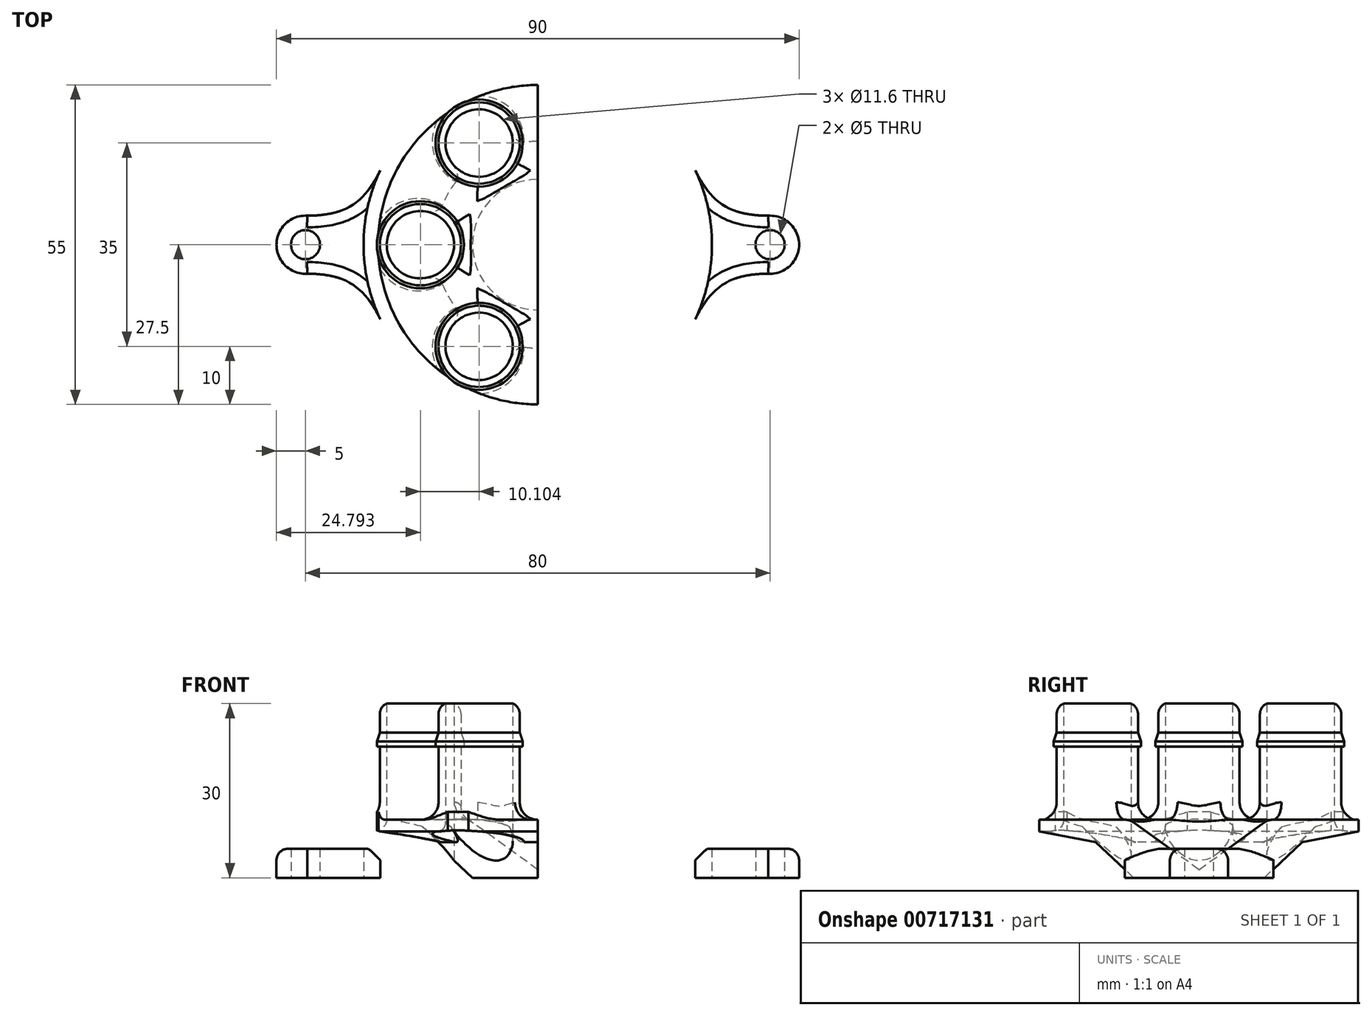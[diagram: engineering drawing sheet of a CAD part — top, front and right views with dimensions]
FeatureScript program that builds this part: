
annotation { "Feature Type Name" : "Feature", "Feature Type Description" : "" }
export const myFeature = defineFeature(function(context is Context, id is Id, definition is map)
    precondition{}
    {
        {
            var Q0;
            Q0=qCreatedBy(makeId("Top.planeOp"),FACE);
            var sketch = newSketch(context, id + "F0", { "sketchPlane" : qUnion([Q0])});
            skLineSegment(sketch, "E0", {"start": v(0, 45.94) * mm, "end": v(0, -54.06) * mm});
            skCircle(sketch, "E1.cCircle", {"center": v(0, 0) * mm, "radius": 17.5 * mm, "construction": true});
            skLineSegment(sketch, "E1.0", {"start": v(-10.1, -17.5) * mm, "end": v(-20.2, 0) * mm, "construction": true});
            skLineSegment(sketch, "E1.1", {"start": v(-20.2, 0) * mm, "end": v(-10.1, 17.5) * mm, "construction": true});
            skLineSegment(sketch, "E1.2", {"start": v(-10.1, 17.5) * mm, "end": v(10.1, 17.5) * mm, "construction": true});
            skLineSegment(sketch, "E1.3", {"start": v(10.1, 17.5) * mm, "end": v(20.2, 0) * mm, "construction": true});
            skLineSegment(sketch, "E1.4", {"start": v(20.2, 0) * mm, "end": v(10.1, -17.5) * mm, "construction": true});
            skLineSegment(sketch, "E1.5", {"start": v(10.1, -17.5) * mm, "end": v(-10.1, -17.5) * mm, "construction": true});
            skPoint(sketch, "E1.0.midPoint", {"position": v(-15.16, -8.75) * mm});
            skCircle(sketch, "E2", {"center": v(-20.2, 0) * mm, "radius": 7 * mm});
            skCircle(sketch, "E3", {"center": v(-10.1, -17.5) * mm, "radius": 7 * mm});
            skCircle(sketch, "E4", {"center": v(-10.1, 17.5) * mm, "radius": 7 * mm});
            skCircle(sketch, "E5", {"center": v(0, 0) * mm, "radius": 27.5 * mm});
            skCircle(sketch, "E6", {"center": v(-20.2, 0) * mm, "radius": 5.8 * mm});
            skCircle(sketch, "E7", {"center": v(-10.1, 17.5) * mm, "radius": 5.8 * mm});
            skCircle(sketch, "E8", {"center": v(-10.1, -17.5) * mm, "radius": 5.8 * mm});
            skCircle(sketch, "E9", {"center": v(0, 0) * mm, "radius": 30 * mm});
            skCircle(sketch, "E10", {"center": v(0, 0) * mm, "radius": 40 * mm, "construction": true});
            skCircle(sketch, "E11", {"center": v(-40, 0) * mm, "radius": 2.5 * mm});
            skCircle(sketch, "E12", {"center": v(-40, 0) * mm, "radius": 5 * mm});
            skFitSpline(sketch, "E13", {"points": [v(-39.69, -5) * mm, v(-27.13, -12.8) * mm], "startDerivative": vector(20.26, -0.15) * mm, "endDerivative": vector(8.15, -16.48) * mm});
            skFitSpline(sketch, "E14.MirrorCS", {"points": [v(-39.69, 5) * mm, v(-27.13, 12.8) * mm], "startDerivative": vector(20.26, 0.15) * mm, "endDerivative": vector(8.15, 16.48) * mm});
            skCircle(sketch, "E15", {"center": v(-10.1, -17.5) * mm, "radius": 7.5 * mm});
            skCircle(sketch, "E16", {"center": v(-20.2, 0) * mm, "radius": 7.5 * mm});
            skCircle(sketch, "E17", {"center": v(-10.1, 17.5) * mm, "radius": 7.5 * mm});
            skSolve(sketch);
        }
        {
            var Q0;
            Q0=makeQuery(id+"F0.imprint","IMPRINT",FACE,{"disambiguationData":[TD([[makeQuery(id+"F0.imprint","IMPRINT",EDGE,{"derivedFrom":sQuery(id+"F0.wireOp",EDGE,"E11")}),-1.0]])]});
            var Q1;
            {var subQ0=sQuery(id+"F0.wireOp",EDGE,"E13");Q1=makeQuery(id+"F0.imprint","IMPRINT",FACE,{"disambiguationData":[TD([[makeQuery(id+"F0.imprint","IMPRINT",EDGE,{"derivedFrom":subQ0}),1.0]])]});}
            extrude(context, id + "F1", {"entities" : qUnion([Q0, Q1]), "depth" : 5 * mm, "offsetDistance" : 25 * mm});
        }
        {
            var Q0;
            {var subQ0=sQuery(id+"F0.wireOp",EDGE,"E9");var subQ2=sQuery(id+"F0.wireOp",EDGE,"E0");var subQ3=makeQuery(id+"F0.imprint","INTERSECT",VERTEX,{"disambiguationData":[OD(0.0)],"derivedFrom":[subQ2,subQ0]});Q0=makeQuery(id+"F0.imprint","IMPRINT",FACE,{"disambiguationData":[TD([[makeQuery(id+"F0.imprint","IMPRINT",EDGE,{"disambiguationData":[TD([[subQ3,-1.0]])],"derivedFrom":subQ2}),-1.0]])]});}
            var Q1;
            {var subQ0=sQuery(id+"F0.wireOp",EDGE,"E17");var subQ1=sQuery(id+"F0.wireOp",EDGE,"E5");var subQ2=makeQuery(id+"F0.imprint","INTERSECT",VERTEX,{"disambiguationData":[OD(0.0)],"derivedFrom":[subQ1,subQ0]});Q1=makeQuery(id+"F0.imprint","IMPRINT",FACE,{"disambiguationData":[TD([[makeQuery(id+"F0.imprint","IMPRINT",EDGE,{"disambiguationData":[TD([[subQ2,-1.0]])],"derivedFrom":subQ1}),-1.0]])]});}
            var Q2;
            {var subQ0=sQuery(id+"F0.wireOp",EDGE,"E16");var subQ1=sQuery(id+"F0.wireOp",EDGE,"E5");var subQ2=makeQuery(id+"F0.imprint","INTERSECT",VERTEX,{"disambiguationData":[OD(0.0)],"derivedFrom":[subQ1,subQ0]});Q2=makeQuery(id+"F0.imprint","IMPRINT",FACE,{"disambiguationData":[TD([[makeQuery(id+"F0.imprint","IMPRINT",EDGE,{"disambiguationData":[TD([[subQ2,-1.0]])],"derivedFrom":subQ1}),-1.0]])]});}
            var Q3;
            {var subQ0=sQuery(id+"F0.wireOp",EDGE,"E15");var subQ1=sQuery(id+"F0.wireOp",EDGE,"E5");var subQ2=makeQuery(id+"F0.imprint","INTERSECT",VERTEX,{"disambiguationData":[OD(0.0)],"derivedFrom":[subQ1,subQ0]});Q3=makeQuery(id+"F0.imprint","IMPRINT",FACE,{"disambiguationData":[TD([[makeQuery(id+"F0.imprint","IMPRINT",EDGE,{"disambiguationData":[TD([[subQ2,-1.0]])],"derivedFrom":subQ1}),-1.0]])]});}
            extrude(context, id + "F2", {"entities" : qUnion([Q0, Q1, Q2, Q3]), "operationType" : NewBodyOperationType.ADD, "depth" : 10 * mm, "offsetDistance" : 25 * mm});
        }
        {
            var Q0;
            Q0=qCreatedBy(makeId("Right.planeOp"),FACE);
            var sketch = newSketch(context, id + "F3", { "sketchPlane" : qUnion([Q0])});
            skLineSegment(sketch, "E18", {"start": v(0, 0) * mm, "end": v(-2.5, 0) * mm});
            skLineSegment(sketch, "E19", {"start": v(-2.5, 0) * mm, "end": v(-27.5, 10) * mm});
            skLineSegment(sketch, "E20", {"start": v(-27.5, 10) * mm, "end": v(0, 10) * mm});
            skLineSegment(sketch, "E21", {"start": v(0, 10) * mm, "end": v(0, 0) * mm});
            skLineSegment(sketch, "E22", {"start": v(-27.5, 10) * mm, "end": v(-27.5, 8) * mm});
            skLineSegment(sketch, "E23", {"start": v(-27.5, 8) * mm, "end": v(-17.8, 6.12) * mm});
            skLineSegment(sketch, "E24", {"start": v(0, 1.4) * mm, "end": v(-11.89, 10) * mm});
            skLineSegment(sketch, "E25", {"start": v(-2.5, 0) * mm, "end": v(-11.23, 0) * mm});
            skLineSegment(sketch, "E26", {"start": v(-11.23, 0) * mm, "end": v(-17.8, 6.12) * mm});
            skSolve(sketch);
        }
        {
            var Q0;
            Q0=makeQuery(id+"F3.imprint","IMPRINT",FACE,{"disambiguationData":[TD([[makeQuery(id+"F3.imprint","IMPRINT",EDGE,{"derivedFrom":sQuery(id+"F3.wireOp",EDGE,"E18")}),-1.0]])]});
            var Q1;
            {var subQ0=sQuery(id+"F3.wireOp",EDGE,"E22");Q1=makeQuery(id+"F3.imprint","IMPRINT",FACE,{"disambiguationData":[TD([[makeQuery(id+"F3.imprint","IMPRINT",EDGE,{"derivedFrom":subQ0}),1.0]])]});}
            var Q2;
            {var subQ0=sQuery(id+"F3.wireOp",EDGE,"E25");Q2=makeQuery(id+"F3.imprint","IMPRINT",FACE,{"disambiguationData":[TD([[makeQuery(id+"F3.imprint","IMPRINT",EDGE,{"derivedFrom":subQ0}),-1.0]])]});}
            var Q3;
            Q3=sQuery(id+"F3.wireOp",EDGE,"E21");
            revolve(context, id + "F4", {"operationType" : NewBodyOperationType.ADD, "surfaceOperationType" : NewSurfaceOperationType.NEW, "entities" : qUnion([Q0, Q1, Q2]), "axis" : qUnion([Q3]), "revolveType" : RevolveType.ONE_DIRECTION, "angle" : 180 * degree});
        }
        {
            var Q0;
            Q0=makeQuery(id+"F0.imprint","IMPRINT",FACE,{"disambiguationData":[TD([[makeQuery(id+"F0.imprint","IMPRINT",EDGE,{"derivedFrom":sQuery(id+"F0.wireOp",EDGE,"E3")}),1.0]])]});
            var Q1;
            Q1=makeQuery(id+"F0.imprint","IMPRINT",FACE,{"disambiguationData":[TD([[makeQuery(id+"F0.imprint","IMPRINT",EDGE,{"derivedFrom":sQuery(id+"F0.wireOp",EDGE,"E2")}),1.0]])]});
            var Q2;
            Q2=makeQuery(id+"F0.imprint","IMPRINT",FACE,{"disambiguationData":[TD([[makeQuery(id+"F0.imprint","IMPRINT",EDGE,{"derivedFrom":sQuery(id+"F0.wireOp",EDGE,"E4")}),1.0]])]});
            extrude(context, id + "F5", {"entities" : qUnion([Q0, Q1, Q2]), "operationType" : NewBodyOperationType.ADD, "depth" : 30 * mm, "offsetDistance" : 25 * mm, "hasSecondDirection" : true, "secondDirectionOppositeDirection" : false, "secondDirectionDepth" : 8 * mm});
        }
        {
            var Q0;
            Q0=makeQuery(id+"F0.imprint","IMPRINT",FACE,{"disambiguationData":[TD([[makeQuery(id+"F0.imprint","IMPRINT",EDGE,{"derivedFrom":sQuery(id+"F0.wireOp",EDGE,"E8")}),1.0]])]});
            var Q1;
            Q1=makeQuery(id+"F0.imprint","IMPRINT",FACE,{"disambiguationData":[TD([[makeQuery(id+"F0.imprint","IMPRINT",EDGE,{"derivedFrom":sQuery(id+"F0.wireOp",EDGE,"E6")}),1.0]])]});
            var Q2;
            Q2=makeQuery(id+"F0.imprint","IMPRINT",FACE,{"disambiguationData":[TD([[makeQuery(id+"F0.imprint","IMPRINT",EDGE,{"derivedFrom":sQuery(id+"F0.wireOp",EDGE,"E7")}),1.0]])]});
            extrude(context, id + "F6", {"entities" : qUnion([Q0, Q1, Q2]), "operationType" : NewBodyOperationType.REMOVE, "depth" : 46.7 * mm, "offsetDistance" : 25 * mm});
        }
        {
            var Q0;
            Q0=makeQuery(id+"F6.boolean.opBoolean","INTERSECT",EDGE,{"derivedFrom":[makeQuery(id+"F4.opRevolve","SWEPT_FACE",FACE,{"disambiguationData":[OSD([sQuery(id+"F3.wireOp",EDGE,"E23")])]}),makeQuery(id+"F6.opExtrude","SWEPT_FACE",FACE,{"disambiguationData":[OSD([sQuery(id+"F0.wireOp",EDGE,"E8")])]})]});
            var Q1;
            Q1=makeQuery(id+"F6.boolean.opBoolean","INTERSECT",EDGE,{"derivedFrom":[makeQuery(id+"F4.opRevolve","SWEPT_FACE",FACE,{"disambiguationData":[OSD([sQuery(id+"F3.wireOp",EDGE,"E23")])]}),makeQuery(id+"F6.opExtrude","SWEPT_FACE",FACE,{"disambiguationData":[OSD([sQuery(id+"F0.wireOp",EDGE,"E6")])]})]});
            var Q2;
            Q2=makeQuery(id+"F6.boolean.opBoolean","INTERSECT",EDGE,{"derivedFrom":[makeQuery(id+"F4.opRevolve","SWEPT_FACE",FACE,{"disambiguationData":[OSD([sQuery(id+"F3.wireOp",EDGE,"E23")])]}),makeQuery(id+"F6.opExtrude","SWEPT_FACE",FACE,{"disambiguationData":[OSD([sQuery(id+"F0.wireOp",EDGE,"E7")])]})]});
            var Q3;
            Q3=makeQuery(id+"F6.boolean.opBoolean","INTERSECT",EDGE,{"derivedFrom":[makeQuery(id+"F4.opRevolve","SWEPT_FACE",FACE,{"disambiguationData":[OSD([sQuery(id+"F3.wireOp",EDGE,"E19")])]}),makeQuery(id+"F6.opExtrude","SWEPT_FACE",FACE,{"disambiguationData":[OSD([sQuery(id+"F0.wireOp",EDGE,"E7")])]})]});
            var Q4;
            Q4=makeQuery(id+"F6.boolean.opBoolean","INTERSECT",EDGE,{"derivedFrom":[makeQuery(id+"F4.opRevolve","SWEPT_FACE",FACE,{"disambiguationData":[OSD([sQuery(id+"F3.wireOp",EDGE,"E19")])]}),makeQuery(id+"F6.opExtrude","SWEPT_FACE",FACE,{"disambiguationData":[OSD([sQuery(id+"F0.wireOp",EDGE,"E6")])]})]});
            var Q5;
            Q5=makeQuery(id+"F6.boolean.opBoolean","INTERSECT",EDGE,{"derivedFrom":[makeQuery(id+"F4.opRevolve","SWEPT_FACE",FACE,{"disambiguationData":[OSD([sQuery(id+"F3.wireOp",EDGE,"E19")])]}),makeQuery(id+"F6.opExtrude","SWEPT_FACE",FACE,{"disambiguationData":[OSD([sQuery(id+"F0.wireOp",EDGE,"E8")])]})]});
            fillet(context, id + "F7", {"entities" : qUnion([Q0, Q1, Q2, Q3, Q4, Q5]), "radius" : 2 * mm, "tangentPropagation" : true, "allowEdgeOverflow" : false});
        }
        {
            var Q0;
            Q0=makeQuery(id+"F4.opRevolve","SWEPT_EDGE",EDGE,{"disambiguationData":[OSD([sQuery(id+"F3.wireOp",EDGE,"E20"),sQuery(id+"F3.wireOp",EDGE,"E24")])]});
            var Q1;
            Q1=makeQuery(id+"F2.opExtrude","CAP_EDGE",EDGE,{"disambiguationData":[OSD([sQuery(id+"F0.wireOp",EDGE,"E9")])],"isStart":false});
            fillet(context, id + "F8", {"entities" : qUnion([Q0, Q1]), "radius" : 3 * mm, "tangentPropagation" : true, "allowEdgeOverflow" : false});
        }
        {
            var Q0;
            Q0=makeQuery(id+"F1.opExtrude","CAP_EDGE",EDGE,{"disambiguationData":[OSD([sQuery(id+"F0.wireOp",EDGE,"E14.MirrorCS")])],"isStart":false});
            var Q1;
            Q1=makeQuery(id+"F1.opExtrude","CAP_EDGE",EDGE,{"disambiguationData":[OSD([sQuery(id+"F0.wireOp",EDGE,"E12")])],"isStart":false});
            var Q2;
            Q2=makeQuery(id+"F1.opExtrude","CAP_EDGE",EDGE,{"disambiguationData":[OSD([sQuery(id+"F0.wireOp",EDGE,"E13")])],"isStart":false});
            fillet(context, id + "F9", {"entities" : qUnion([Q0, Q1, Q2]), "radius" : 2 * mm, "tangentPropagation" : true, "allowEdgeOverflow" : false});
        }
        {
            var Q0;
            Q0=makeQuery(id+"F5.opExtrude","CAP_EDGE",EDGE,{"disambiguationData":[OSD([sQuery(id+"F0.wireOp",EDGE,"E4")])],"isStart":false});
            var Q1;
            Q1=makeQuery(id+"F5.opExtrude","CAP_EDGE",EDGE,{"disambiguationData":[OSD([sQuery(id+"F0.wireOp",EDGE,"E2")])],"isStart":false});
            var Q2;
            Q2=makeQuery(id+"F5.opExtrude","CAP_EDGE",EDGE,{"disambiguationData":[OSD([sQuery(id+"F0.wireOp",EDGE,"E3")])],"isStart":false});
            fillet(context, id + "F10", {"entities" : qUnion([Q0, Q1, Q2]), "radius" : 2 * mm, "tangentPropagation" : true, "allowEdgeOverflow" : false});
        }
        {
            var Q0;
            Q0=makeQuery(id+"F0.imprint","IMPRINT",FACE,{"disambiguationData":[TD([[makeQuery(id+"F0.imprint","IMPRINT",EDGE,{"derivedFrom":sQuery(id+"F0.wireOp",EDGE,"E3")}),-1.0]])]});
            var Q1;
            Q1=makeQuery(id+"F0.imprint","IMPRINT",FACE,{"disambiguationData":[TD([[makeQuery(id+"F0.imprint","IMPRINT",EDGE,{"derivedFrom":sQuery(id+"F0.wireOp",EDGE,"E2")}),-1.0]])]});
            var Q2;
            Q2=makeQuery(id+"F0.imprint","IMPRINT",FACE,{"disambiguationData":[TD([[makeQuery(id+"F0.imprint","IMPRINT",EDGE,{"derivedFrom":sQuery(id+"F0.wireOp",EDGE,"E4")}),-1.0]])]});
            var Q3;
            {var subQ0=sQuery(id+"F0.wireOp",EDGE,"E15");var subQ1=sQuery(id+"F0.wireOp",EDGE,"E5");var subQ2=makeQuery(id+"F0.imprint","INTERSECT",VERTEX,{"disambiguationData":[OD(0.0)],"derivedFrom":[subQ1,subQ0]});Q3=makeQuery(id+"F0.imprint","IMPRINT",FACE,{"disambiguationData":[TD([[makeQuery(id+"F0.imprint","IMPRINT",EDGE,{"disambiguationData":[TD([[subQ2,-1.0]])],"derivedFrom":subQ1}),-1.0]])]});}
            var Q4;
            {var subQ0=sQuery(id+"F0.wireOp",EDGE,"E16");var subQ1=sQuery(id+"F0.wireOp",EDGE,"E5");var subQ2=makeQuery(id+"F0.imprint","INTERSECT",VERTEX,{"disambiguationData":[OD(0.0)],"derivedFrom":[subQ1,subQ0]});Q4=makeQuery(id+"F0.imprint","IMPRINT",FACE,{"disambiguationData":[TD([[makeQuery(id+"F0.imprint","IMPRINT",EDGE,{"disambiguationData":[TD([[subQ2,-1.0]])],"derivedFrom":subQ1}),-1.0]])]});}
            var Q5;
            {var subQ0=sQuery(id+"F0.wireOp",EDGE,"E17");var subQ1=sQuery(id+"F0.wireOp",EDGE,"E5");var subQ2=makeQuery(id+"F0.imprint","INTERSECT",VERTEX,{"disambiguationData":[OD(0.0)],"derivedFrom":[subQ1,subQ0]});Q5=makeQuery(id+"F0.imprint","IMPRINT",FACE,{"disambiguationData":[TD([[makeQuery(id+"F0.imprint","IMPRINT",EDGE,{"disambiguationData":[TD([[subQ2,-1.0]])],"derivedFrom":subQ1}),-1.0]])]});}
            extrude(context, id + "F11", {"entities" : qUnion([Q0, Q1, Q2, Q3, Q4, Q5]), "operationType" : NewBodyOperationType.ADD, "depth" : 25 * mm, "offsetDistance" : 25 * mm, "hasSecondDirection" : true, "secondDirectionOppositeDirection" : false, "secondDirectionDepth" : 22.6 * mm});
        }
        {
            var Q0;
            Q0=makeQuery(id+"F5.boolean.opBoolean","INTERSECT",EDGE,{"derivedFrom":[makeQuery(id+"F4.boolean.opBoolean","MERGE",FACE,{"derivedFrom":[makeQuery(id+"F2.opExtrude","CAP_FACE",FACE,{"disambiguationData":[OSD([sQuery(id+"F0.wireOp",EDGE,"E0"),sQuery(id+"F0.wireOp",EDGE,"E5"),sQuery(id+"F0.wireOp",EDGE,"E9")])],"isStart":false}),makeQuery(id+"F4.opRevolve","SWEPT_FACE",FACE,{"disambiguationData":[OSD([sQuery(id+"F3.wireOp",EDGE,"E20")])]})]}),makeQuery(id+"F5.opExtrude","SWEPT_FACE",FACE,{"disambiguationData":[OSD([sQuery(id+"F0.wireOp",EDGE,"E3")])]})]});
            var Q1;
            Q1=makeQuery(id+"F5.boolean.opBoolean","INTERSECT",EDGE,{"derivedFrom":[makeQuery(id+"F4.boolean.opBoolean","MERGE",FACE,{"derivedFrom":[makeQuery(id+"F2.opExtrude","CAP_FACE",FACE,{"disambiguationData":[OSD([sQuery(id+"F0.wireOp",EDGE,"E0"),sQuery(id+"F0.wireOp",EDGE,"E5"),sQuery(id+"F0.wireOp",EDGE,"E9")])],"isStart":false}),makeQuery(id+"F4.opRevolve","SWEPT_FACE",FACE,{"disambiguationData":[OSD([sQuery(id+"F3.wireOp",EDGE,"E20")])]})]}),makeQuery(id+"F5.opExtrude","SWEPT_FACE",FACE,{"disambiguationData":[OSD([sQuery(id+"F0.wireOp",EDGE,"E2")])]})]});
            var Q2;
            Q2=makeQuery(id+"F5.boolean.opBoolean","INTERSECT",EDGE,{"derivedFrom":[makeQuery(id+"F4.boolean.opBoolean","MERGE",FACE,{"derivedFrom":[makeQuery(id+"F2.opExtrude","CAP_FACE",FACE,{"disambiguationData":[OSD([sQuery(id+"F0.wireOp",EDGE,"E0"),sQuery(id+"F0.wireOp",EDGE,"E5"),sQuery(id+"F0.wireOp",EDGE,"E9")])],"isStart":false}),makeQuery(id+"F4.opRevolve","SWEPT_FACE",FACE,{"disambiguationData":[OSD([sQuery(id+"F3.wireOp",EDGE,"E20")])]})]}),makeQuery(id+"F5.opExtrude","SWEPT_FACE",FACE,{"disambiguationData":[OSD([sQuery(id+"F0.wireOp",EDGE,"E4")])]})]});
            fillet(context, id + "F12", {"entities" : qUnion([Q0, Q1, Q2]), "radius" : 3 * mm, "tangentPropagation" : true, "allowEdgeOverflow" : false});
        }
        {
            var Q0;
            Q0=makeQuery(id+"F11.opExtrude","CAP_EDGE",EDGE,{"disambiguationData":[OSD([sQuery(id+"F0.wireOp",EDGE,"E17")])],"isStart":false});
            var Q1;
            Q1=makeQuery(id+"F11.opExtrude","CAP_EDGE",EDGE,{"disambiguationData":[OSD([sQuery(id+"F0.wireOp",EDGE,"E16")])],"isStart":false});
            var Q2;
            Q2=makeQuery(id+"F11.opExtrude","CAP_EDGE",EDGE,{"disambiguationData":[OSD([sQuery(id+"F0.wireOp",EDGE,"E15")])],"isStart":false});
            chamfer(context, id + "F13", {"entities" : qUnion([Q0, Q1, Q2]), "chamferType" : ChamferType.TWO_OFFSETS, "width1" : 0.5 * mm, "oppositeDirection" : false, "width2" : 1.5 * mm, "tangentPropagation" : true});
        }
        {
            var Q0;
            Q0=makeQuery(id+"F1.opExtrude","SWEPT_BODY",BODY,{"disambiguationData":[OSD([sQuery(id+"F0.wireOp",EDGE,"E9"),sQuery(id+"F0.wireOp",EDGE,"E11"),sQuery(id+"F0.wireOp",EDGE,"E12"),sQuery(id+"F0.wireOp",EDGE,"E13"),sQuery(id+"F0.wireOp",EDGE,"E14.MirrorCS")])]});
            var Q1;
            Q1=qCreatedBy(makeId("Right.planeOp"),FACE);
            mirror(context, id + "F14", {"operationType" : NewBodyOperationType.ADD, "entities" : qUnion([Q0]), "mirrorPlane" : qUnion([Q1])});
        }
    });
